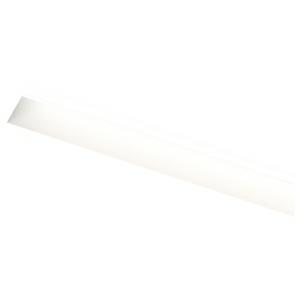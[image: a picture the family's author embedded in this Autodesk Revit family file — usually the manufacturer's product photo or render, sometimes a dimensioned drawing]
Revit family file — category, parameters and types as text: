
# Revit family: groove_l_880_rl_led_16w_3000k_1023lm_cri80_130-0470_acf8
name_source: partatom
category: Leuchten
revit_build: Autodesk Revit 2016 (Build: 20190508_0715(x64)
units: mm (PartAtom-declared; Revit-internal decimal feet)

## family parameters
Basisbauteil = Fläche
Beim Laden mit Abzugskörper schneiden = Nein
Bemaßung runder Anschluss = Durchmesser verwenden
Gemeinsam genutzt = Nein
Lichtquelle = Nein
Raumberechnungspunkt = Nein
Teiletyp = Normal

## types (1)
- 130-0470- (3 x LED, 710 lm, 5.1 W, 3000K)
    Beschreibung = The rimless luminaire GROOVE from the familiy GROOVE consists of aluminum-extruded profile. Charming SOFT-EDGE design ensure unparalleled styling. The ballast is integrated and allows for an operation with 220-240V (50.60Hz). GROOVE (# 130-0470) ist not dimmable (on/off). The luminaire with direct illumination and corresponds to protection class SK1 at IP20.
    CIE Flux Codes = 59 87 97 100 49
    Color Rendering = 1B/80…89
    Color Temperature = 3000K
    Height = 0 mm  [stored 0 ft]
    Hersteller = Prolicht
    Lamp Light Flux = 710 lm
    Lamp Power = 5.1 W
    Lamp count = 3
    Lampe = 3 x LED
    Length = 880 mm
    Luminous efficacy = 67 lm/W
    ModVariant = Nein
    Modell = 130-0470
    Mounting Place = Ceiling
    Mounting Type = Recessed
    Number of Poles = 1
    OnlyDefault = Ja
    Power Factor = 1
    Product Name = GROOVE L=880 RL LED 16W 3000K 1023lm CRI80
    Product group = Trimless recessed profile lights
    ProductGroupID = 413
    Protection Class = Protection class
    Protection Degree = Degree of protection
    RLX_Detail_Level = 1
    RlxData = <blob elided: 133137 chars, md5=82010fc9>
    Scheinlast = 15 VA
    Socket = socket
    Standby Power = 0 W
    System Light Flux = 1027 lm
    System Power = 15 W
    Typenbild = 130-0470.jpg
    URL = http://relux.com
    VarID = 130-0470-
    Voltage = 0 V
    Vorgabe-Ansicht = 1800 mm
    Weight = 0.00 kg
    Width = 75 mm

note: [stored X ft] marks values corroborated as IEEE doubles in the binary element streams (Revit-internal decimal feet)

## geometry (parser evidence)
native form markers: Blend x4, Sweep x14
no freeform markers — native parametric forms only
